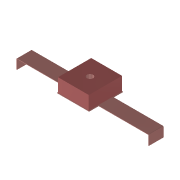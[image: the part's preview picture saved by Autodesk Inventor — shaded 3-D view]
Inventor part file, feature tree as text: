
AUTODESK INVENTOR PART (.ipt)
format: ipt  version: 2022 (Build 260153000, 153)  size: 117,248 bytes
history: native  units: mm
features: extrude x1, sketch x1, other x1
ambient origin geometry x8: Origin, YZ Plane, XZ Plane, XY Plane, X Axis, Y Axis, Z Axis, Center Point
bodies: Volumenkörper1 (feature_tree)
feature tree (3):
  extrude  "Extrusion1"  [1 undecoded]
  sketch  "Skizze1"  dims[d0=10.0mm d1=0.0mm]
  other  "Boss-Extrude1"
note: 1 required parameter value undecoded (feature->parameter linkage not recoverable at this tier; creation-order binding heuristic only, values carry confidence <= 0.55)
